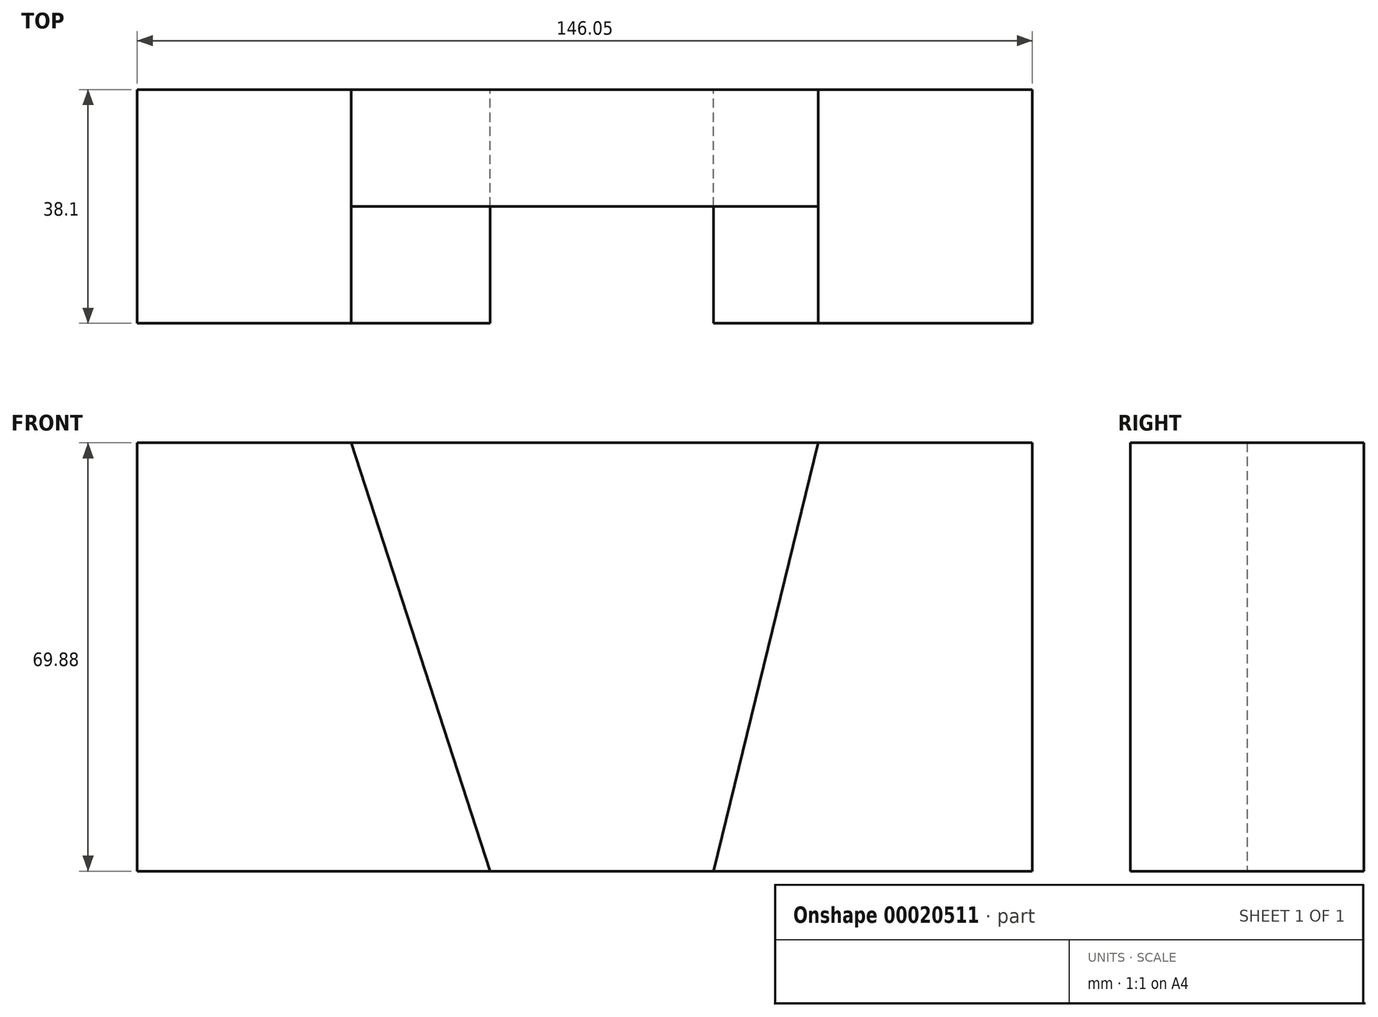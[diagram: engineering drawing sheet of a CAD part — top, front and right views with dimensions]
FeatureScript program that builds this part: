
annotation { "Feature Type Name" : "Feature", "Feature Type Description" : "" }
export const myFeature = defineFeature(function(context is Context, id is Id, definition is map)
    precondition{}
    {
        {
            var Q0;
            Q0=qCreatedBy(makeId("Front.planeOp"),FACE);
            var sketch = newSketch(context, id + "F0", { "sketchPlane" : qUnion([Q0])});
            skLineSegment(sketch, "E0.bottom", {"start": v(-78.67, 29.38) * mm, "end": v(-43.74, 29.38) * mm});
            skLineSegment(sketch, "E0.top", {"start": v(-78.67, -40.5) * mm, "end": v(67.38, -40.5) * mm});
            skLineSegment(sketch, "E0.left", {"start": v(-78.67, 29.38) * mm, "end": v(-78.67, -40.5) * mm});
            skLineSegment(sketch, "E0.right", {"start": v(67.38, 29.38) * mm, "end": v(67.38, -40.5) * mm});
            skLineSegment(sketch, "E1", {"start": v(-43.74, 29.38) * mm, "end": v(-21.07, -40.5) * mm});
            skLineSegment(sketch, "E2", {"start": v(32.46, 29.38) * mm, "end": v(15.36, -40.5) * mm});
            skLineSegment(sketch, "E3.trimOffspring", {"start": v(32.46, 29.38) * mm, "end": v(67.38, 29.38) * mm});
            skLineSegment(sketch, "E4", {"start": v(-43.74, 29.38) * mm, "end": v(32.46, 29.38) * mm});
            skSolve(sketch);
        }
        {
            var Q0;
            Q0=makeQuery(id+"F0.imprint","IMPRINT",FACE,{"disambiguationData":[TD([[makeQuery(id+"F0.imprint","IMPRINT",EDGE,{"derivedFrom":sQuery(id+"F0.wireOp",EDGE,"E0.bottom")}),-1.0]])]});
            extrude(context, id + "F1", {"entities" : qUnion([Q0]), "depth" : 38.1 * mm});
        }
        {
            var Q0;
            {var subQ1=sQuery(id+"F0.wireOp",EDGE,"E0.right");Q0=makeQuery(id+"F0.imprint","IMPRINT",FACE,{"disambiguationData":[TD([[makeQuery(id+"F0.imprint","IMPRINT",EDGE,{"derivedFrom":subQ1}),-1.0]])]});}
            extrude(context, id + "F2", {"entities" : qUnion([Q0]), "depth" : 38.1 * mm});
        }
        {
            var Q0;
            {var subQ1=sQuery(id+"F0.wireOp",EDGE,"E1");Q0=makeQuery(id+"F0.imprint","IMPRINT",FACE,{"disambiguationData":[TD([[makeQuery(id+"F0.imprint","IMPRINT",EDGE,{"derivedFrom":subQ1}),1.0]])]});}
            extrude(context, id + "F3", {"entities" : qUnion([Q0]), "depth" : 19.05 * mm});
        }
    });
